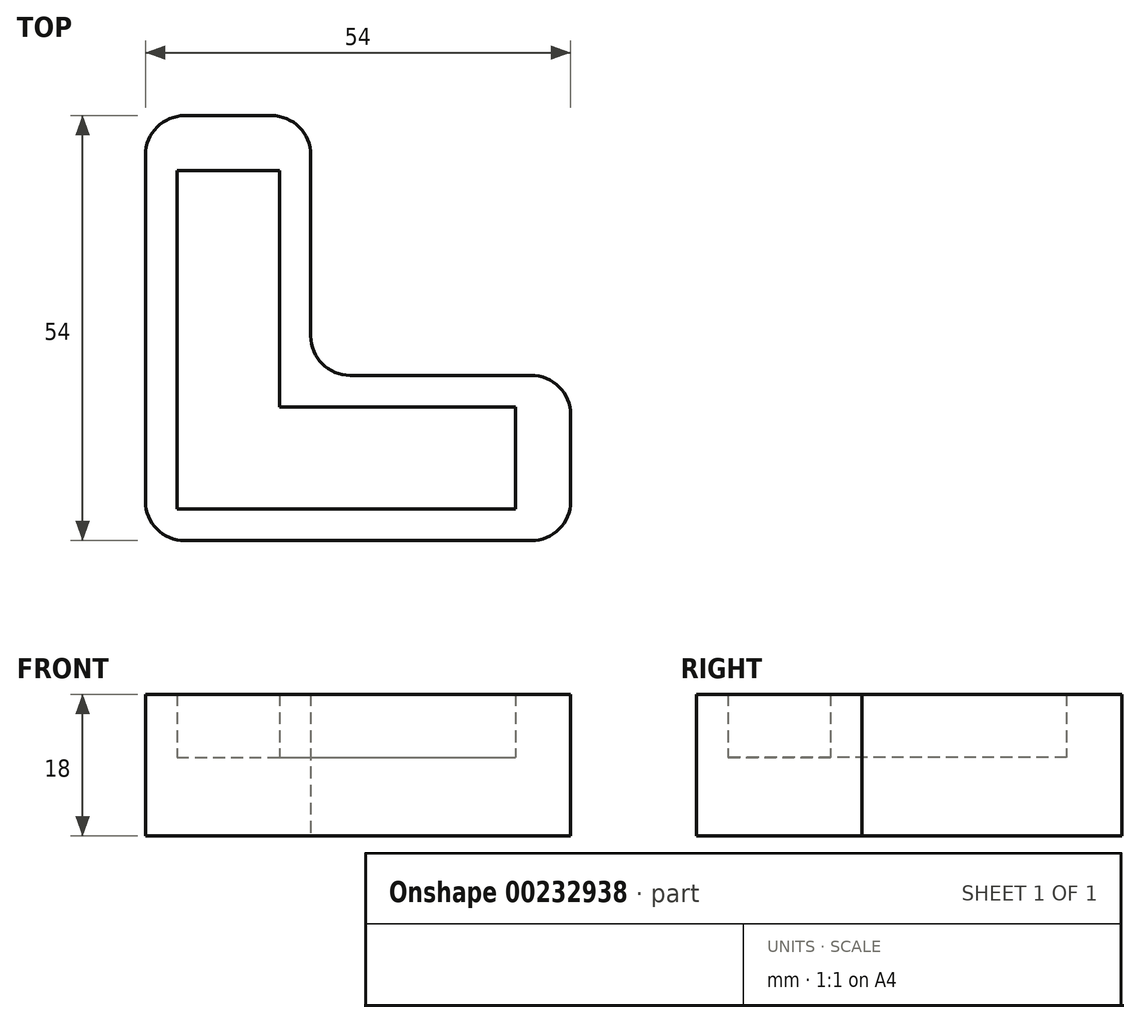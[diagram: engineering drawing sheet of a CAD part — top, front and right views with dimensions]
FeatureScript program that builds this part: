
annotation { "Feature Type Name" : "Feature", "Feature Type Description" : "" }
export const myFeature = defineFeature(function(context is Context, id is Id, definition is map)
    precondition{}
    {
        {
            var Q0;
            Q0=qCreatedBy(makeId("Top.planeOp"),FACE);
            var sketch = newSketch(context, id + "F0", { "sketchPlane" : qUnion([Q0])});
            skLineSegment(sketch, "E0.bottom", {"start": v(0, 0) * mm, "end": v(54, 0) * mm});
            skLineSegment(sketch, "E0.top", {"start": v(0, 54) * mm, "end": v(21, 54) * mm});
            skLineSegment(sketch, "E0.left", {"start": v(0, 0) * mm, "end": v(0, 54) * mm});
            skLineSegment(sketch, "E0.right", {"start": v(54, 0) * mm, "end": v(54, 21) * mm});
            skLineSegment(sketch, "E1", {"start": v(4, 54) * mm, "end": v(4, 4) * mm});
            skLineSegment(sketch, "E2", {"start": v(4, 4) * mm, "end": v(54, 4) * mm});
            skLineSegment(sketch, "E3", {"start": v(47, 4) * mm, "end": v(47, 17) * mm});
            skLineSegment(sketch, "E4", {"start": v(4, 47) * mm, "end": v(17, 47) * mm});
            skLineSegment(sketch, "E5", {"start": v(17, 47) * mm, "end": v(17, 17) * mm});
            skLineSegment(sketch, "E6", {"start": v(17, 17) * mm, "end": v(47, 17) * mm});
            skLineSegment(sketch, "E7", {"start": v(54, 21) * mm, "end": v(21, 21) * mm});
            skLineSegment(sketch, "E8", {"start": v(21, 21) * mm, "end": v(21, 54) * mm});
            skSolve(sketch);
        }
        {
            var Q0;
            {var subQ5=sQuery(id+"F0.wireOp",EDGE,"E0.bottom");Q0=makeQuery(id+"F0.imprint","IMPRINT",FACE,{"disambiguationData":[TD([[makeQuery(id+"F0.imprint","IMPRINT",EDGE,{"derivedFrom":subQ5}),1.0]])]});}
            var Q1;
            {var subQ7=sQuery(id+"F0.wireOp",EDGE,"E3");Q1=makeQuery(id+"F0.imprint","IMPRINT",FACE,{"disambiguationData":[TD([[makeQuery(id+"F0.imprint","IMPRINT",EDGE,{"derivedFrom":subQ7}),-1.0]])]});}
            extrude(context, id + "F1", {"entities" : qUnion([Q0, Q1]), "depth" : 18 * mm, "offsetDistance" : 25 * mm});
        }
        {
            var Q0;
            {var subQ0=sQuery(id+"F0.wireOp",EDGE,"E3");Q0=makeQuery(id+"F0.imprint","IMPRINT",FACE,{"disambiguationData":[TD([[makeQuery(id+"F0.imprint","IMPRINT",EDGE,{"derivedFrom":subQ0}),1.0]])]});}
            extrude(context, id + "F2", {"entities" : qUnion([Q0]), "operationType" : NewBodyOperationType.ADD, "depth" : 10 * mm, "offsetDistance" : 25 * mm});
        }
        {
            var Q0;
            Q0=makeQuery(id+"F1.opExtrude","SWEPT_EDGE",EDGE,{"disambiguationData":[OSD([sQuery(id+"F0.wireOp",EDGE,"E0.bottom"),sQuery(id+"F0.wireOp",EDGE,"E0.left")])]});
            var Q1;
            Q1=makeQuery(id+"F1.opExtrude","SWEPT_EDGE",EDGE,{"disambiguationData":[OSD([sQuery(id+"F0.wireOp",EDGE,"E0.top"),sQuery(id+"F0.wireOp",EDGE,"E0.left")])]});
            var Q2;
            Q2=makeQuery(id+"F1.opExtrude","SWEPT_EDGE",EDGE,{"disambiguationData":[OSD([sQuery(id+"F0.wireOp",EDGE,"E0.bottom"),sQuery(id+"F0.wireOp",EDGE,"E0.right")])]});
            var Q3;
            Q3=makeQuery(id+"F1.opExtrude","SWEPT_EDGE",EDGE,{"disambiguationData":[OSD([sQuery(id+"F0.wireOp",EDGE,"E0.right"),sQuery(id+"F0.wireOp",EDGE,"E7")])]});
            var Q4;
            Q4=makeQuery(id+"F1.opExtrude","SWEPT_EDGE",EDGE,{"disambiguationData":[OSD([sQuery(id+"F0.wireOp",EDGE,"E0.top"),sQuery(id+"F0.wireOp",EDGE,"E8")])]});
            var Q5;
            Q5=makeQuery(id+"F1.opExtrude","SWEPT_EDGE",EDGE,{"disambiguationData":[OSD([sQuery(id+"F0.wireOp",EDGE,"E7"),sQuery(id+"F0.wireOp",EDGE,"E8")])]});
            fillet(context, id + "F3", {"entities" : qUnion([Q0, Q1, Q2, Q3, Q4, Q5]), "tangentPropagation" : true, "radius" : 5 * mm, "defaultsChanged" : false, "vertexSettings" : [], "allowEdgeOverflow" : false});
        }
    });
